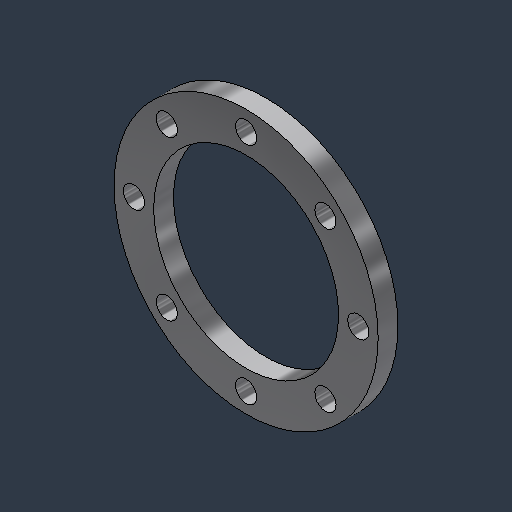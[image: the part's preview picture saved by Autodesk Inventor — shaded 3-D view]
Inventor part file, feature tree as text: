
AUTODESK INVENTOR PART (.ipt)
format: ipt  version: 2024.3 (Build 283343000, 343)  size: 142,336 bytes
history: native  units: mm (DEFAULTED — no unit token found)
features: sketch x2, extrude x1, hole x1, pattern_circular x1
ambient origin geometry x8: Origin, YZ Plane, XZ Plane, XY Plane, X Axis, Y Axis, Z Axis, Center Point
bodies: Solid1 (feature_tree)
feature tree (5):
  extrude  "Extrusion1"  Depth=9.525mm
  hole  "Hole1"  [1 undecoded]
  pattern_circular  "Circular Pattern1"  Count=8 Angle=360.0deg
  sketch  "Sketch2"  dims[d0=44.45mm d1=9.525mm]
  sketch  "Sketch3"  dims[d2=4.7625mm d3=0.0mm d4=26.9875mm d5=5.1054mm d6=9.652mm d7=9.779mm d8=1.9558mm d9=14.3117mm d10=25.4mm d11=20.594885mm d12=80.0mm d13=360.0deg]
note: 1 required parameter value undecoded (feature->parameter linkage not recoverable at this tier; creation-order binding heuristic only, values carry confidence <= 0.55)
